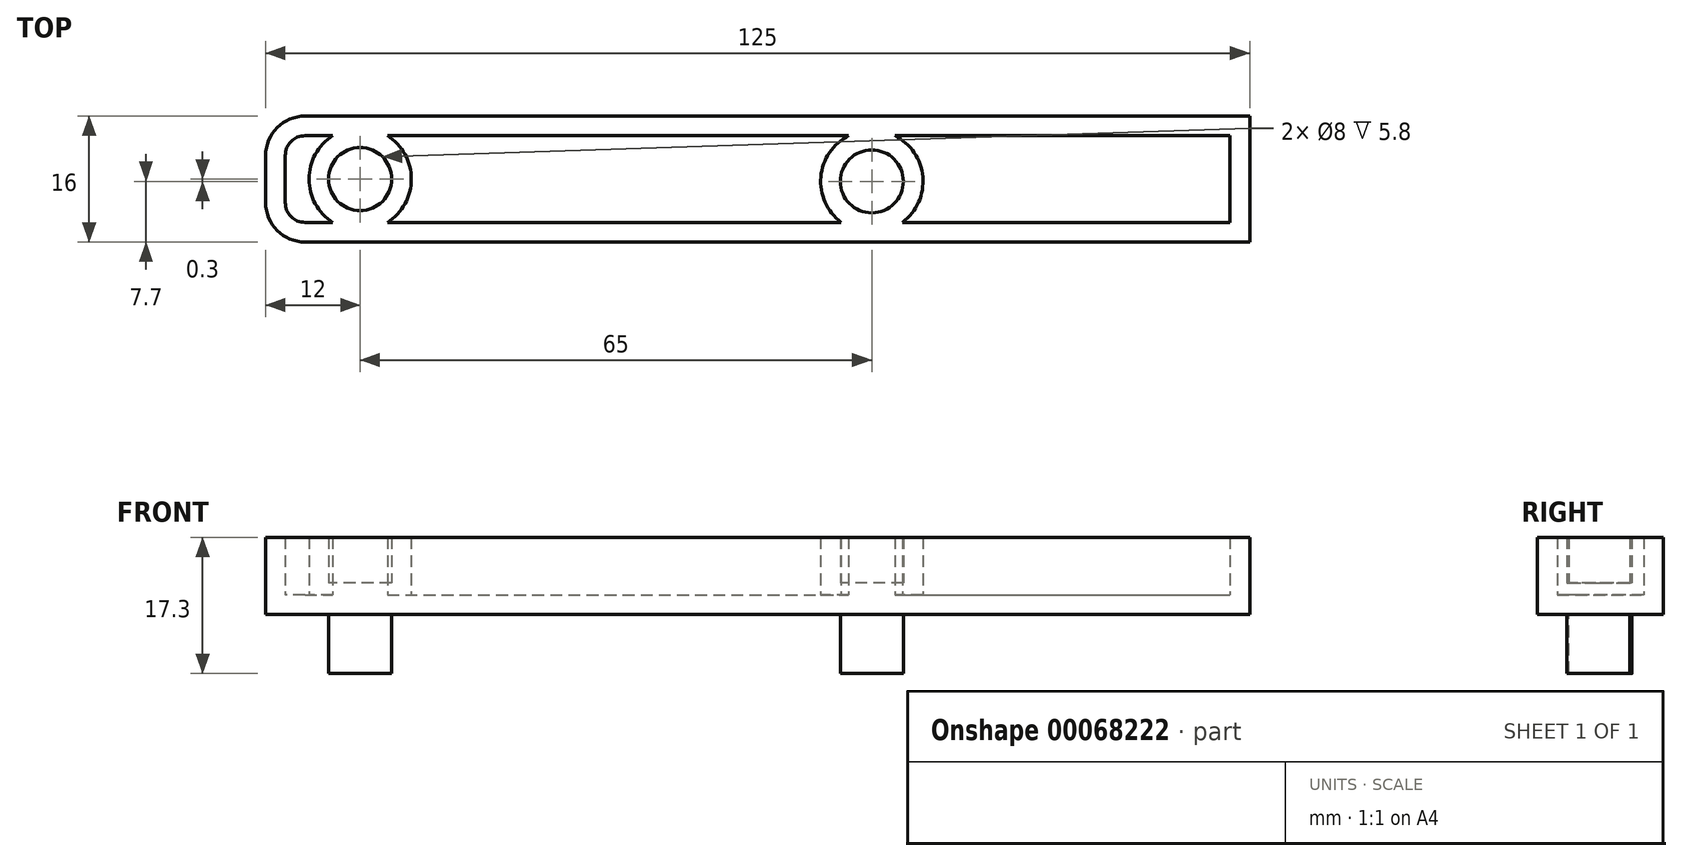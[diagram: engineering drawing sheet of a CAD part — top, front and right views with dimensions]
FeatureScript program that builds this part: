
annotation { "Feature Type Name" : "Feature", "Feature Type Description" : "" }
export const myFeature = defineFeature(function(context is Context, id is Id, definition is map)
    precondition{}
    {
        {
            var Q0;
            Q0=qCreatedBy(makeId("Top.planeOp"),FACE);
            var sketch = newSketch(context, id + "F0", { "sketchPlane" : qUnion([Q0])});
            skLineSegment(sketch, "E0.bottom", {"start": v(-62.5, 8) * mm, "end": v(62.5, 8) * mm});
            skLineSegment(sketch, "E0.top", {"start": v(-62.5, -8) * mm, "end": v(62.5, -8) * mm});
            skLineSegment(sketch, "E0.left", {"start": v(-62.5, 8) * mm, "end": v(-62.5, -8) * mm});
            skLineSegment(sketch, "E0.right", {"start": v(62.5, 8) * mm, "end": v(62.5, -8) * mm});
            skPoint(sketch, "E0.middle", {"position": v(0, 0) * mm});
            skCircle(sketch, "E1", {"center": v(-50.5, 0) * mm, "radius": 4 * mm});
            skCircle(sketch, "E2", {"center": v(14.5, -0.3) * mm, "radius": 4 * mm});
            skSolve(sketch);
        }
        {
            var Q0;
            Q0 = qSketchRegion(id + "F0", true);
            extrude(context, id + "F1", {"entities" : qUnion([Q0]), "depth" : 9.8 * mm});
        }
        {
            var Q0;
            Q0=makeQuery(id+"F0.imprint","IMPRINT",FACE,{"disambiguationData":[TD([[makeQuery(id+"F0.imprint","IMPRINT",EDGE,{"derivedFrom":sQuery(id+"F0.wireOp",EDGE,"E1")}),1.0]])]});
            var Q1;
            Q1=makeQuery(id+"F0.imprint","IMPRINT",FACE,{"disambiguationData":[TD([[makeQuery(id+"F0.imprint","IMPRINT",EDGE,{"derivedFrom":sQuery(id+"F0.wireOp",EDGE,"E2")}),1.0]])]});
            extrude(context, id + "F2", {"entities" : qUnion([Q0, Q1]), "operationType" : NewBodyOperationType.ADD, "oppositeDirection" : true, "depth" : 7.5 * mm, "hasSecondDirection" : true, "secondDirectionOppositeDirection" : false, "secondDirectionDepth" : 4 * mm});
        }
        {
            var Q0;
            Q0=makeQuery(id+"F1.opExtrude","SWEPT_EDGE",EDGE,{"disambiguationData":[OSD([sQuery(id+"F0.wireOp",EDGE,"E0.bottom"),sQuery(id+"F0.wireOp",EDGE,"E0.left")])]});
            var Q1;
            Q1=makeQuery(id+"F1.opExtrude","SWEPT_EDGE",EDGE,{"disambiguationData":[OSD([sQuery(id+"F0.wireOp",EDGE,"E0.top"),sQuery(id+"F0.wireOp",EDGE,"E0.left")])]});
            fillet(context, id + "F3", {"entities" : qUnion([Q0, Q1]), "radius" : 5 * mm, "tangentPropagation" : true, "allowEdgeOverflow" : false});
        }
        {
            var Q0;
            Q0=makeQuery(id+"F1.opExtrude","CAP_FACE",FACE,{"disambiguationData":[OSD([sQuery(id+"F0.wireOp",EDGE,"E0.bottom"),sQuery(id+"F0.wireOp",EDGE,"E0.top"),sQuery(id+"F0.wireOp",EDGE,"E0.left"),sQuery(id+"F0.wireOp",EDGE,"E0.right"),sQuery(id+"F0.wireOp",EDGE,"E1"),sQuery(id+"F0.wireOp",EDGE,"E2")])],"isStart":false});
            shell(context, id + "F4", {"entities" : qUnion([Q0]), "thickness" : 2.5 * mm});
        }
    });
